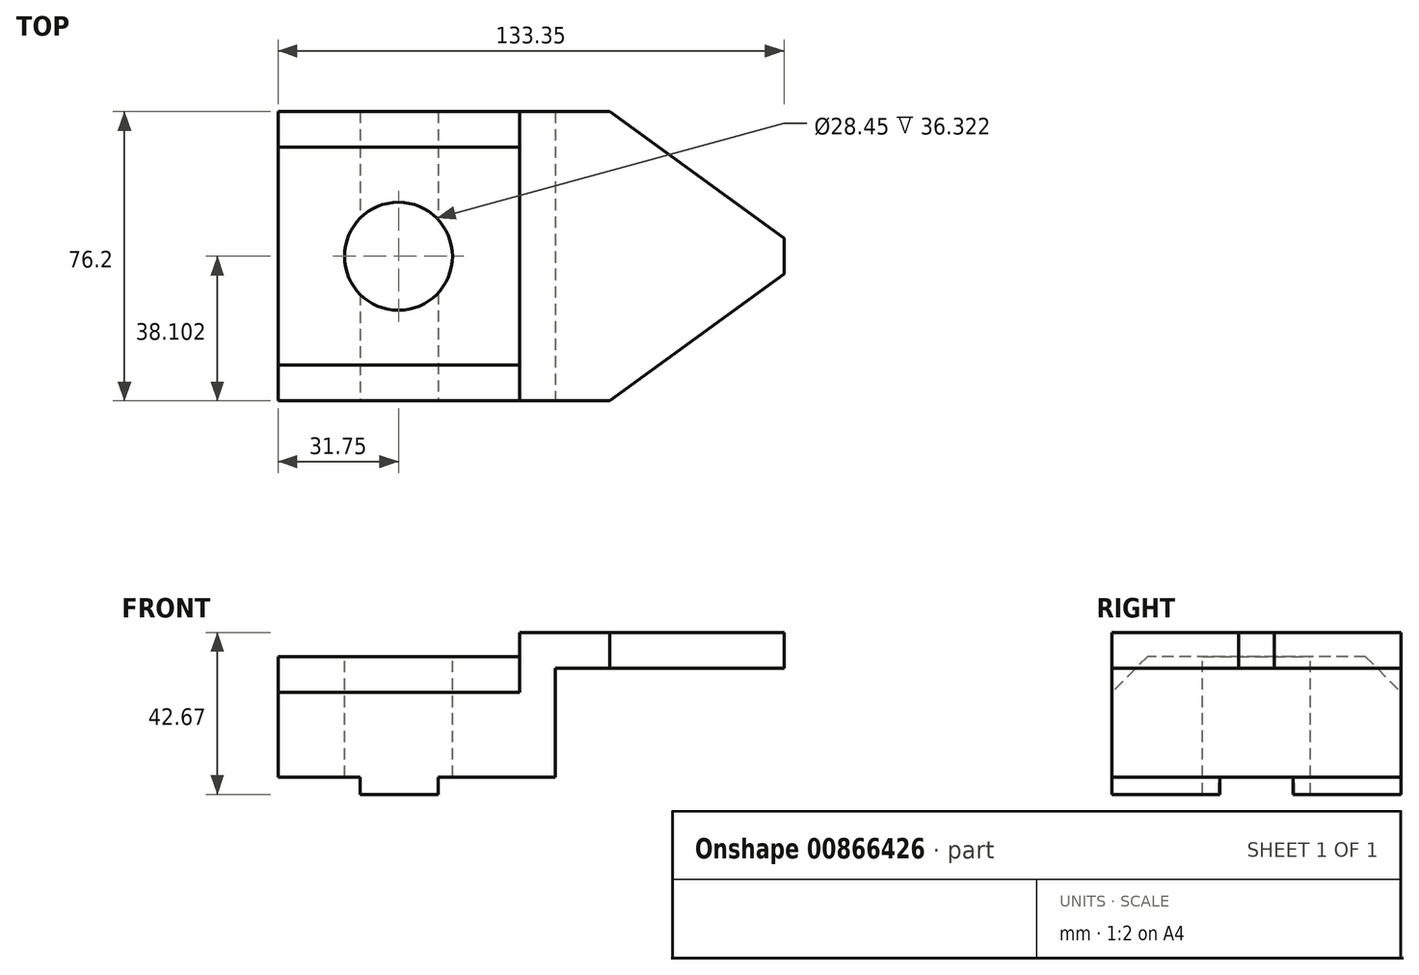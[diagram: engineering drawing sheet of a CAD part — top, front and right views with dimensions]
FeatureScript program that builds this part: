
annotation { "Feature Type Name" : "Feature", "Feature Type Description" : "" }
export const myFeature = defineFeature(function(context is Context, id is Id, definition is map)
    precondition{}
    {
        {
            var Q0;
            Q0=qCreatedBy(makeId("Top.planeOp"),FACE);
            var sketch = newSketch(context, id + "F0", { "sketchPlane" : qUnion([Q0])});
            skLineSegment(sketch, "E0", {"start": v(-88.44, 50.75) * mm, "end": v(-88.44, -25.45) * mm});
            skLineSegment(sketch, "E1", {"start": v(-88.44, -25.45) * mm, "end": v(44.9, -25.45) * mm});
            skLineSegment(sketch, "E2", {"start": v(-88.44, 50.75) * mm, "end": v(44.9, 50.75) * mm});
            skLineSegment(sketch, "E3", {"start": v(44.9, 50.75) * mm, "end": v(44.9, -25.45) * mm});
            skSolve(sketch);
        }
        {
            var Q0;
            Q0=makeQuery(id+"F0.imprint","IMPRINT",FACE,{"disambiguationData":[TD([[makeQuery(id+"F0.imprint","IMPRINT",EDGE,{"derivedFrom":sQuery(id+"F0.wireOp",EDGE,"E0")}),1.0]])]});
            extrude(context, id + "F1", {"entities" : qUnion([Q0]), "depth" : 42.67 * mm, "offsetDistance" : 25.4 * mm});
        }
        {
            var Q0;
            Q0=makeQuery(id+"F1.opExtrude","SWEPT_FACE",FACE,{"disambiguationData":[OSD([sQuery(id+"F0.wireOp",EDGE,"E1")])]});
            var sketch = newSketch(context, id + "F2", { "sketchPlane" : qUnion([Q0])});
            skLineSegment(sketch, "E4", {"start": v(44.9, 33.27) * mm, "end": v(-24.69, 33.27) * mm});
            skLineSegment(sketch, "E5", {"start": v(-66.85, 0) * mm, "end": v(-66.85, 4.57) * mm});
            skLineSegment(sketch, "E6", {"start": v(-66.85, 4.57) * mm, "end": v(-88.44, 4.57) * mm});
            skLineSegment(sketch, "E7", {"start": v(-66.85, 0) * mm, "end": v(-46.28, 0) * mm});
            skLineSegment(sketch, "E8", {"start": v(-46.28, 0) * mm, "end": v(-46.28, 4.57) * mm});
            skLineSegment(sketch, "E9", {"start": v(-46.28, 4.57) * mm, "end": v(-24.69, 4.57) * mm});
            skLineSegment(sketch, "E10", {"start": v(-24.69, 4.57) * mm, "end": v(-24.69, 33.27) * mm});
            skSolve(sketch);
        }
        {
            var Q0;
            {var subQ0=sQuery(id+"F2.wireOp",EDGE,"E5");Q0=makeQuery(id+"F2.imprint","IMPRINT",FACE,{"disambiguationData":[TD([[makeQuery(id+"F2.imprint","IMPRINT",EDGE,{"derivedFrom":subQ0}),1.0]])]});}
            var Q1;
            {var subQ1=sQuery(id+"F2.wireOp",EDGE,"E4");Q1=makeQuery(id+"F2.imprint","IMPRINT",FACE,{"disambiguationData":[TD([[makeQuery(id+"F2.imprint","IMPRINT",EDGE,{"derivedFrom":subQ1}),1.0]])]});}
            extrude(context, id + "F3", {"entities" : qUnion([Q0, Q1]), "operationType" : NewBodyOperationType.REMOVE, "endBound" : BoundingType.THROUGH_ALL, "oppositeDirection" : true, "depth" : 25.4 * mm, "offsetDistance" : 25.4 * mm});
        }
        {
            var Q0;
            Q0=makeQuery(id+"F1.opExtrude","CAP_FACE",FACE,{"disambiguationData":[OSD([sQuery(id+"F0.wireOp",EDGE,"E0"),sQuery(id+"F0.wireOp",EDGE,"E1"),sQuery(id+"F0.wireOp",EDGE,"E2"),sQuery(id+"F0.wireOp",EDGE,"E3")])],"isStart":false});
            var sketch = newSketch(context, id + "F4", { "sketchPlane" : qUnion([Q0])});
            skLineSegment(sketch, "E11", {"start": v(-1.06, 50.75) * mm, "end": v(-1.06, -25.45) * mm});
            skLineSegment(sketch, "E12", {"start": v(44.9, 12.65) * mm, "end": v(44.9, 17.35) * mm});
            skLineSegment(sketch, "E13", {"start": v(44.9, 12.65) * mm, "end": v(44.9, 7.95) * mm});
            skLineSegment(sketch, "E14", {"start": v(-1.06, 50.75) * mm, "end": v(44.9, 17.35) * mm});
            skLineSegment(sketch, "E15", {"start": v(44.9, 7.95) * mm, "end": v(-1.06, -25.45) * mm});
            skLineSegment(sketch, "E16", {"start": v(-1.06, 50.75) * mm, "end": v(-24.69, 50.75) * mm});
            skLineSegment(sketch, "E17", {"start": v(-24.69, 50.75) * mm, "end": v(-24.69, -25.45) * mm});
            skLineSegment(sketch, "E18", {"start": v(-24.69, -25.45) * mm, "end": v(-1.06, -25.45) * mm});
            skSolve(sketch);
        }
        {
            var Q0;
            {var subQ0=sQuery(id+"F4.wireOp",EDGE,"E14");Q0=makeQuery(id+"F4.imprint","IMPRINT",FACE,{"disambiguationData":[TD([[makeQuery(id+"F4.imprint","IMPRINT",EDGE,{"derivedFrom":subQ0}),1.0]])]});}
            var Q1;
            {var subQ0=sQuery(id+"F4.wireOp",EDGE,"E15");Q1=makeQuery(id+"F4.imprint","IMPRINT",FACE,{"disambiguationData":[TD([[makeQuery(id+"F4.imprint","IMPRINT",EDGE,{"derivedFrom":subQ0}),1.0]])]});}
            extrude(context, id + "F5", {"entities" : qUnion([Q0, Q1]), "operationType" : NewBodyOperationType.REMOVE, "endBound" : BoundingType.THROUGH_ALL, "oppositeDirection" : true, "depth" : 25.4 * mm, "offsetDistance" : 25.4 * mm});
        }
        {
            var Q0;
            {var subQ0=sQuery(id+"F4.wireOp",EDGE,"E17");Q0=makeQuery(id+"F4.imprint","IMPRINT",FACE,{"disambiguationData":[TD([[makeQuery(id+"F4.imprint","IMPRINT",EDGE,{"derivedFrom":subQ0}),-1.0]])]});}
            extrude(context, id + "F6", {"entities" : qUnion([Q0]), "operationType" : NewBodyOperationType.REMOVE, "oppositeDirection" : true, "depth" : 6.35 * mm, "offsetDistance" : 25.4 * mm});
        }
        {
            var Q0;
            Q0=makeQuery(id+"F3.boolean.opBoolean","COPY",FACE,{"derivedFrom":makeQuery(id+"F3.opExtrude","SWEPT_FACE",FACE,{"disambiguationData":[OSD([sQuery(id+"F2.wireOp",EDGE,"E10")])]})});
            extrude(context, id + "F7", {"entities" : qUnion([Q0]), "operationType" : NewBodyOperationType.ADD, "depth" : 9.4 * mm, "offsetDistance" : 25.4 * mm});
        }
        {
            var Q0;
            Q0=makeQuery(id+"F1.opExtrude","SWEPT_FACE",FACE,{"disambiguationData":[OSD([sQuery(id+"F0.wireOp",EDGE,"E0")])]});
            var sketch = newSketch(context, id + "F8", { "sketchPlane" : qUnion([Q0])});
            skLineSegment(sketch, "E19", {"start": v(-41.35, 36.32) * mm, "end": v(-41.35, 4.57) * mm});
            skLineSegment(sketch, "E20", {"start": v(16.05, 36.32) * mm, "end": v(16.05, 4.57) * mm});
            skLineSegment(sketch, "E21", {"start": v(-41.35, 36.32) * mm, "end": v(-60, 36.32) * mm, "construction": true});
            skLineSegment(sketch, "E22", {"start": v(16.05, 36.32) * mm, "end": v(39.52, 36.32) * mm, "construction": true});
            skLineSegment(sketch, "E23", {"start": v(-41.35, 36.32) * mm, "end": v(-50.75, 26.92) * mm});
            skLineSegment(sketch, "E24", {"start": v(16.05, 36.32) * mm, "end": v(25.45, 26.92) * mm});
            skSolve(sketch);
        }
        {
            var Q0;
            {var subQ0=sQuery(id+"F8.wireOp",EDGE,"E23");Q0=makeQuery(id+"F8.imprint","IMPRINT",FACE,{"disambiguationData":[TD([[makeQuery(id+"F8.imprint","IMPRINT",EDGE,{"derivedFrom":subQ0}),-1.0]])]});}
            var Q1;
            {var subQ0=sQuery(id+"F8.wireOp",EDGE,"E24");Q1=makeQuery(id+"F8.imprint","IMPRINT",FACE,{"disambiguationData":[TD([[makeQuery(id+"F8.imprint","IMPRINT",EDGE,{"derivedFrom":subQ0}),1.0]])]});}
            extrude(context, id + "F9", {"entities" : qUnion([Q0, Q1]), "operationType" : NewBodyOperationType.REMOVE, "oppositeDirection" : true, "depth" : 63.75 * mm, "offsetDistance" : 25.4 * mm});
        }
        {
            var Q0;
            Q0=makeQuery(id+"F6.boolean.opBoolean","COPY",FACE,{"derivedFrom":makeQuery(id+"F6.opExtrude","CAP_FACE",FACE,{"disambiguationData":[OSD([sQuery(id+"F0.wireOp",EDGE,"E0"),sQuery(id+"F0.wireOp",EDGE,"E1"),sQuery(id+"F0.wireOp",EDGE,"E2"),sQuery(id+"F4.wireOp",EDGE,"E17")])],"isStart":false})});
            var sketch = newSketch(context, id + "F10", { "sketchPlane" : qUnion([Q0])});
            skCircle(sketch, "E25", {"center": v(-56.7, 12.65) * mm, "radius": 14.22 * mm});
            skSolve(sketch);
        }
        {
            var Q0;
            Q0=makeQuery(id+"F10.imprint","IMPRINT",FACE,{"disambiguationData":[TD([[makeQuery(id+"F10.imprint","IMPRINT",EDGE,{"derivedFrom":sQuery(id+"F10.wireOp",EDGE,"E25")}),1.0]])]});
            extrude(context, id + "F11", {"entities" : qUnion([Q0]), "operationType" : NewBodyOperationType.REMOVE, "endBound" : BoundingType.THROUGH_ALL, "oppositeDirection" : true, "depth" : 25.4 * mm, "offsetDistance" : 25.4 * mm});
        }
    });
